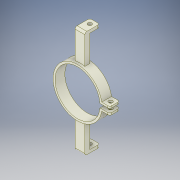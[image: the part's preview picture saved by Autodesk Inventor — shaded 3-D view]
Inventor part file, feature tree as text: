
AUTODESK INVENTOR PART (.ipt)
format: ipt  version: 2019 (Build 230136000, 136)  size: 199,168 bytes
history: native  units: mm
features: extrude x5, sketch x5, plane x2, mirror x1, fillet x1, projected_geometry x1
ambient origin geometry x8: Origin, YZ Plane, XZ Plane, XY Plane, X Axis, Y Axis, Z Axis, Center Point
bodies: Solid1 (feature_tree)
feature tree (15):
  extrude  "Extrusion1"  Depth=50.0mm
  extrude  "Extrusion2"  Depth=2.0mm
  plane  "Work Plane1"
  extrude  "Extrusion3"  Depth=4.0mm
  extrude  "Extrusion4"  Depth=20.0mm
  plane  "Work Plane2"
  extrude  "Extrusion5"  Depth=10.0mm TaperAngle=0.0deg
  mirror  "Mirror2"
  fillet  "Fillet1"  Radius=15.0mm
  sketch  "Sketch1"  dims[d0=46.0mm d1=50.0mm]
  sketch  "Sketch2"  dims[d7=2.0mm d9=2.0mm]
  projected_geometry  "Projected Loop1"
  sketch  "Sketch3"  dims[d10=10.0mm d11=0.0mm d12=4.0mm]
  sketch  "Sketch4"  dims[d13=8.5mm d14=0.0mm d15=20.0mm]
  sketch  "Sketch5"  dims[d19=27.5mm d20=0.0mm d23=10.0mm d24=0.0mm d27=15.0mm d28=3.0mm d29=4.0mm d30=4.0mm d31=0.0mm d32=2.0mm]
